# Revit family: Layout-Teknion-Modular_Cabinets_Printing_Center-R2018
name_source: partatom
category: Furniture Systems
revit_build: Autodesk Revit 2018 (Build: 20190510_1515(x64)
units: mm (PartAtom-declared; Revit-internal decimal feet)

## family parameters
Always vertical = Yes
Cut with Voids When Loaded = No
OmniClass Number = 23.40.70.14.64.21
OmniClass Title = Systems Furniture
Part Type = Normal
Room Calculation Point = No
Round Connector Dimension = Use Diameter
Shared = Yes
Work Plane-Based = No

## types (1)
- Layout 02 - Printing Center
    Assembly Code = E2020200
    Description = 17'-6" x 12'-6" Overall
    Manufacturer = Teknion
    Manufacturer Fax = 416.661.4586
    Model = Layout 02 - Modular Cabinet - Printing Center
    Product Line = Modular Cabinets
    Product Page URL = https://www.teknion.com
    Series = Modular Cabinets
    Sustainability Data = https://www.teknion.com
    URL = www.teknion.com
    Unit Weight URL = http://www.teknion.com
    Warranty = http://www.teknion.com

## geometry (parser evidence)
native form markers: Blend x8, Extrusion x1, Sweep x20
no freeform markers — native parametric forms only
